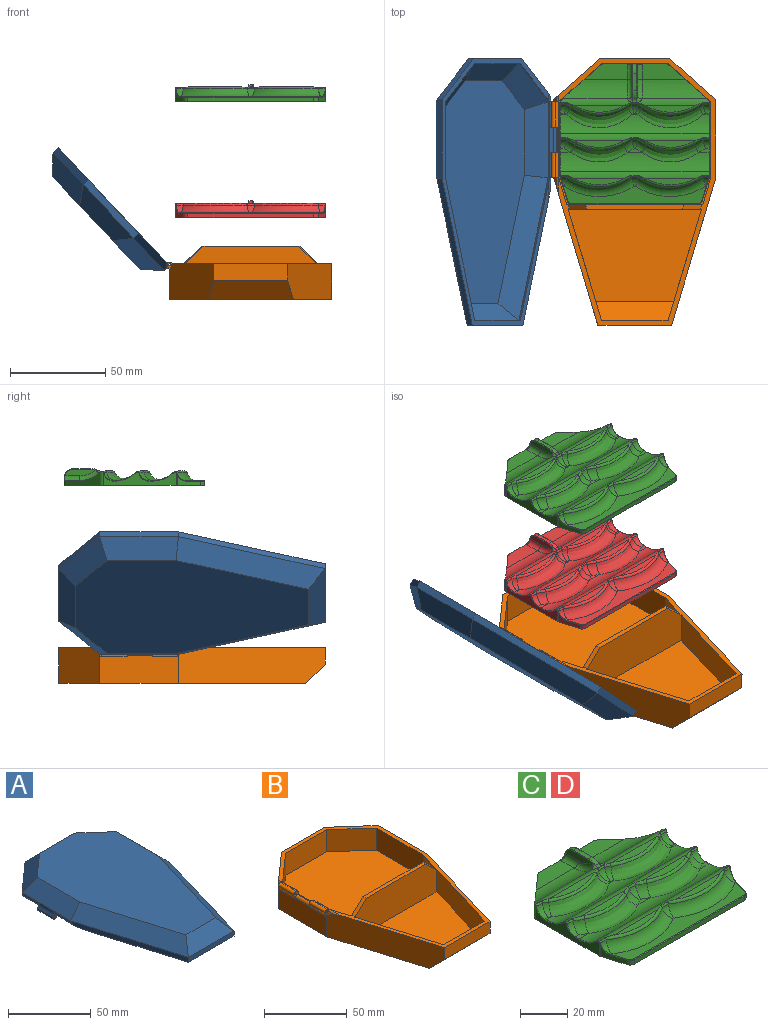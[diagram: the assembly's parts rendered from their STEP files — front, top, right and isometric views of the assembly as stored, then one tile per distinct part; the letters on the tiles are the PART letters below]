
ASSEMBLY  parts=4 mates=3
PART A: 45 faces, bbox 89.1x142.7x17.2 mm
  f0: plane 0.12x0mm, normal (0,1,0), area 0mm2, adj f8,f42
  f1: plane 0.12x0mm, normal (0,-1,0), area 0mm2, adj f8,f42
  f2: cylinder r=1.42mm len=13.33mm, axis (0,-1,0), area 61.4mm2, adj f4,f40,f41,f42
  f3: cylinder r=0.64mm len=13.33mm, axis (0,-1,0), area 53.2mm2, adj f40,f41
  f4: cylinder r=5.08mm len=13.33mm, axis (0,1,0), area 26.1mm2, adj f2,f5,f40,f41
  f5: plane 40x1.11mm, normal (1,0,0), area 43.4mm2, adj f4,f16,f22,f27,f40,f41,f43,f44
  f6: plane 140.08x81.78mm, normal (0,0,-1), area 825.5mm2, adj f7,f9,f10,f11,f12,f13,f14,f16
  f7: plane 24.08x21.4mm, normal (-0.66,0.75,0), area 115.7mm2, adj f6,f8,f14,f35,f44
  f8: plane 41.51x0.35mm, normal (-1,0,0), area 12.9mm2, adj f0,f1,f7,f9,f37,f42,f43,f44
  f9: plane 79.74x25.73mm, normal (-0.96,-0.29,0), area 289.2mm2, adj f6,f8,f10,f39,f43
  f10: plane 38.78x3.65mm, normal (0,-1,0), area 141.5mm2, adj f6,f9,f11,f38
  f11: plane 77.17x23.15mm, normal (0.96,-0.29,0), area 294.1mm2, adj f6,f10,f12,f36
  f12: plane 41.51x3.65mm, normal (1,0,0), area 151.5mm2, adj f6,f11,f13,f34
  f13: plane 24.07x21.4mm, normal (0.66,0.75,0), area 117.6mm2, adj f6,f12,f14,f32
  f14: plane 36.93x3.65mm, normal (0,1,0), area 134.8mm2, adj f6,f7,f13,f33
  f15: plane 122.3x67.3mm, normal (0,0,1), area 6472mm2, adj f32,f33,f34,f35,f36,f37,f38,f39
  f16: plane 22.64x20.14mm, normal (0.66,-0.75,0), area 33.4mm2, adj f5,f6,f17,f25,f44
  f17: plane 35x1.11mm, normal (0,-1,0), area 38.9mm2, adj f6,f16,f18,f24
  f18: plane 22.5x20mm, normal (-0.66,-0.75,0), area 33.4mm2, adj f6,f17,f19,f26
  f19: plane 40x1.11mm, normal (-1,0,0), area 44.4mm2, adj f6,f18,f20,f28
  f20: plane 75x22.5mm, normal (-0.96,0.29,0), area 86.9mm2, adj f6,f19,f21,f30
  f21: plane 35x1.11mm, normal (0,1,0), area 38.9mm2, adj f6,f20,f22,f31
  f22: plane 75.35x22.85mm, normal (0.96,0.29,0), area 86.9mm2, adj f5,f6,f21,f29,f43
  f23: plane 117.22x62.22mm, normal (0,0,-1), area 5673.4mm2, adj f24,f25,f26,f27,f28,f29,f30,f31
  f24: plane 35x8.89mm, normal (0,-0.71,-0.71), area 397.5mm2, adj f17,f23,f25,f26
  f25: plane 25.88x23.99mm, normal (0.47,-0.53,-0.71), area 332.1mm2, adj f16,f23,f24,f27
  f26: plane 25.88x23.99mm, normal (-0.47,-0.53,-0.71), area 332.1mm2, adj f18,f23,f24,f28
  f27: plane 40x8.89mm, normal (0.71,0,-0.71), area 469.6mm2, adj f5,f23,f25,f29
  f28: plane 40x8.89mm, normal (-0.71,0,-0.71), area 469.6mm2, adj f19,f23,f26,f30
  f29: plane 76.3x29.11mm, normal (0.68,0.2,-0.71), area 934.7mm2, adj f22,f23,f27,f31
  f30: plane 76.3x29.11mm, normal (-0.68,0.2,-0.71), area 934.7mm2, adj f20,f23,f28,f31
  f31: plane 35x8.89mm, normal (0,0.71,-0.71), area 356.9mm2, adj f21,f23,f29,f30
  f32: plane 27.45x25.39mm, normal (0.47,0.53,0.71), area 358.6mm2, adj f13,f15,f33,f34
  f33: plane 36.93x8.89mm, normal (0,0.71,0.71), area 421.8mm2, adj f14,f15,f32,f35
  f34: plane 41.51x8.89mm, normal (0.71,0,0.71), area 488.6mm2, adj f12,f15,f32,f36
  f35: plane 27.45x25.39mm, normal (-0.47,0.53,0.71), area 358.6mm2, adj f7,f15,f33,f37
  f36: plane 78.47x29.76mm, normal (0.68,-0.2,0.71), area 963.1mm2, adj f11,f15,f34,f38
  f37: plane 41.51x8.89mm, normal (-0.71,0,0.71), area 488.6mm2, adj f8,f15,f35,f39
  f38: plane 38.78x8.89mm, normal (0,-0.71,0.71), area 404.4mm2, adj f10,f15,f36,f39
  f39: plane 78.47x29.76mm, normal (-0.68,-0.2,0.71), area 963.1mm2, adj f9,f15,f37,f38
  f40: plane 5.49x4.09mm, normal (0,1,0), area 7.4mm2, adj f2,f3,f4,f5,f42,f44
  f41: plane 5.48x4.09mm, normal (0,-1,0), area 7.4mm2, adj f2,f3,f4,f5,f42,f43
  f42: cylinder r=5.08mm len=13.33mm, axis (0,-1,0), area 45.6mm2, adj f0,f1,f2,f8,f40,f41
  f43: bspline ~27.18x3.3mm, area 92mm2, adj f5,f6,f8,f9,f22,f41
  f44: bspline ~19.15x3.3mm, area 72.6mm2, adj f5,f6,f7,f8,f16,f40
PART B: 49 faces, bbox 86.5x140.1x27.9 mm
  f0: plane 58.42x17.53mm, normal (-0.96,0.29,0), area 943.3mm2, adj f22,f25,f31,f45,f47
  f1: plane 16.35x14.04mm, normal (0.96,0.29,0), area 239.7mm2, adj f8,f24,f31,f46
  f2: plane 5.48x3.85mm, normal (0,-1,0), area 6.5mm2, adj f3,f4,f5,f29,f32,f35,f36,f39
  f3: plane 41.51x14.93mm, normal (-1,0,0), area 599.5mm2, adj f2,f9,f10,f11,f26,f27,f28,f29
  f4: cylinder r=1.42mm len=13.33mm, axis (0,-1,0), area 54.6mm2, adj f2,f27,f29,f36
  f5: cylinder r=0.64mm len=13.33mm, axis (0,-1,0), area 53.2mm2, adj f2,f27
  f6: cylinder r=1.42mm len=13.33mm, axis (0,-1,0), area 54.6mm2, adj f9,f26,f28,f37
  f7: cylinder r=0.64mm len=13.33mm, axis (0,-1,0), area 53.2mm2, adj f9,f26
  f8: plane 40x16.35mm, normal (1,0,0), area 626.6mm2, adj f1,f17,f26,f27,f30,f31,f46
  f9: plane 5.48x3.85mm, normal (0,1,0), area 6.5mm2, adj f3,f6,f7,f28,f33,f34,f37,f38
  f10: plane 24.07x21.4mm, normal (-0.66,0.75,0), area 604.4mm2, adj f3,f16,f31,f33,f34,f38,f44
  f11: plane 77.17x23.15mm, normal (-0.96,-0.29,0), area 1457.3mm2, adj f3,f12,f31,f32,f35,f39,f44,f48
  f12: plane 38.78x8.73mm, normal (0,-1,0), area 338.5mm2, adj f11,f13,f31,f48
  f13: plane 77.17x23.15mm, normal (0.96,-0.29,0), area 1468mm2, adj f12,f14,f31,f44,f48
  f14: plane 41.51x18.89mm, normal (1,0,0), area 784.2mm2, adj f13,f15,f31,f44
  f15: plane 24.07x21.4mm, normal (0.66,0.75,0), area 608.5mm2, adj f14,f16,f31,f44
  f16: plane 36.93x18.89mm, normal (0,1,0), area 697.6mm2, adj f10,f15,f31,f44
  f17: plane 22.5x20mm, normal (0.66,-0.75,0), area 492.2mm2, adj f8,f18,f31,f46
  f18: plane 35x16.35mm, normal (0,-1,0), area 572.2mm2, adj f17,f19,f31,f46
  f19: plane 22.5x20mm, normal (-0.66,-0.75,0), area 492.2mm2, adj f18,f20,f31,f46
  f20: plane 40x16.35mm, normal (-1,0,0), area 654mm2, adj f19,f21,f31,f46
  f21: plane 16.35x14.04mm, normal (-0.96,0.29,0), area 239.7mm2, adj f20,f24,f31,f46
  f22: plane 35x6.19mm, normal (0,1,0), area 216.7mm2, adj f0,f23,f31,f47
  f23: plane 58.42x17.53mm, normal (0.96,0.29,0), area 943.3mm2, adj f22,f25,f31,f45,f47
  f24: plane 71.58x25.34mm, normal (0,1,0), area 1720.4mm2, adj f1,f21,f31,f41,f42,f43,f46
  f25: plane 70.05x25.34mm, normal (0,-1,0), area 1681.8mm2, adj f0,f23,f31,f41,f42,f43,f45
  f26: plane 5.48x3.96mm, normal (0,-1,0), area 9.4mm2, adj f3,f6,f7,f8,f28,f30,f31,f34
  f27: plane 5.48x3.96mm, normal (0,1,0), area 9.4mm2, adj f3,f4,f5,f8,f29,f30,f31,f35
  f28: cylinder r=5.08mm len=13.33mm, axis (0,-1,0), area 45.6mm2, adj f3,f6,f9,f26
  f29: cylinder r=5.08mm len=13.33mm, axis (0,-1,0), area 45.6mm2, adj f2,f3,f4,f27
  f30: plane 13.33x0.64mm, normal (0,0,1), area 8.5mm2, adj f8,f26,f27,f40
  f31: plane 140.08x82.62mm, normal (0,0,1), area 840.3mm2, adj f0,f1,f8,f10,f11,f12,f13,f14
  f32: cylinder r=5.08mm len=2.99mm, axis (0,-1,0), area 3.6mm2, adj f2,f3,f11,f39
  f33: cylinder r=5.08mm len=2.71mm, axis (0,1,0), area 3.9mm2, adj f3,f9,f10,f38
  f34: cylinder r=1.27mm len=16.66mm, axis (0,1,0), area 4.7mm2, adj f9,f10,f26,f31,f37,f38
  f35: cylinder r=1.27mm len=21.92mm, axis (0,1,0), area 10.2mm2, adj f2,f11,f27,f31,f36,f39
  f36: cylinder r=2.54mm len=13.33mm, axis (0,-1,0), area 22.6mm2, adj f2,f4,f27,f35
  f37: cylinder r=2.54mm len=13.33mm, axis (0,-1,0), area 22.6mm2, adj f6,f9,f26,f34
  f38: cylinder r=5.08mm len=2.27mm, axis (0,1,0), area 2.3mm2, adj f9,f10,f33,f34
  f39: cylinder r=5.08mm len=4.6mm, axis (0,-1,0), area 4.3mm2, adj f2,f11,f32,f35
  f40: cylinder r=1.91mm len=13.33mm, axis (0,-1,0), area 39.9mm2, adj f3,f26,f27,f30
  f41: plane 51.79x2.54mm, normal (0,0,1), area 129.6mm2, adj f24,f25,f42,f43
  f42: plane 10.15x8.99mm, normal (-0.68,-0.2,0.71), area 33.7mm2, adj f24,f25,f31,f41
  f43: plane 10.15x8.99mm, normal (0.68,-0.2,0.71), area 33.7mm2, adj f24,f25,f31,f41
  f44: plane 129.92x85.08mm, normal (0,0,-1), area 9191.4mm2, adj f3,f10,f11,f13,f14,f15,f16,f48
  f45: plane 70.05x48.26mm, normal (0,0,1), area 2682mm2, adj f0,f23,f25,f47
  f46: plane 80x74.04mm, normal (0,0,1), area 5414.1mm2, adj f1,f8,f17,f18,f19,f20,f21,f24
  f47: plane 41.1x10.16mm, normal (0,0.71,0.71), area 546.7mm2, adj f0,f22,f23,f45
  f48: plane 44.88x10.16mm, normal (0,-0.71,-0.71), area 601mm2, adj f11,f12,f13,f44
PART C: 152 faces, bbox 84.9x79x9.7 mm
  f0: plane 75.15x9.18mm, normal (0,0,1), area 389.9mm2, adj f27,f28,f29,f30,f31,f116,f119,f121
  f1: plane 12.35x5.29mm, normal (-0.96,-0.29,0), area 33.7mm2, adj f13,f82,f89,f125,f127
  f2: cylinder r=15.24mm len=34.12mm, axis (1,0,0), area 316.2mm2, adj f3,f14,f75,f148,f149
  f3: plane 22.81x8.29mm, normal (0,0,1), area 150.1mm2, adj f2,f14,f15,f85,f150,f151
  f4: plane 26.96x3.76mm, normal (0,0,1), area 67.3mm2, adj f53,f75
  f5: plane 26.91x3.64mm, normal (0,0,1), area 65.6mm2, adj f64,f65,f67,f74
  f6: plane 26.91x3.53mm, normal (0,0,1), area 64.1mm2, adj f72,f73
  f7: plane 3.32x0.83mm, normal (0,0,1), area 2.2mm2, adj f25,f42,f44,f94
  f8: plane 3.33x0.83mm, normal (0,0,1), area 1.6mm2, adj f25,f47,f48,f49
  f9: plane 5.69x2.1mm, normal (0,0,1), area 7.9mm2, adj f24,f32,f33,f126
  f10: plane 5.69x2.1mm, normal (0,0,1), area 7.9mm2, adj f24,f39,f40,f101
  f11: plane 3.32x0.83mm, normal (0,0,1), area 2.2mm2, adj f25,f41,f43,f113
  f12: plane 22.81x8.29mm, normal (0,0,1), area 150.1mm2, adj f15,f16,f26,f86,f141,f142
  f13: plane 78.73x73.79mm, normal (0,0,-1), area 5309.7mm2, adj f1,f14,f15,f16,f17,f18,f19,f81
  f14: plane 20.55x18.27mm, normal (-0.66,0.75,0), area 91.1mm2, adj f2,f3,f13,f75,f84,f85
  f15: plane 32.66x4.42mm, normal (0,1,0), area 88.9mm2, adj f3,f12,f13,f80,f85,f86,f141,f151
  f16: plane 20.55x18.27mm, normal (0.66,0.75,0), area 91.1mm2, adj f12,f13,f26,f75,f86,f87
  f17: plane 38.11x7.17mm, normal (1,0,0), area 142.3mm2, adj f13,f87,f88,f93,f94,f95,f97,f99
  f18: plane 12.35x5.29mm, normal (0.96,-0.29,0), area 33.7mm2, adj f13,f83,f88,f114,f116
  f19: plane 38.11x7.17mm, normal (-1,0,0), area 142.3mm2, adj f13,f84,f89,f111,f113,f115,f117,f122
  f20: plane 8.07x2.1mm, normal (0,0,1), area 8.8mm2, adj f24,f35,f36,f37
  f21: plane 26.96x3.76mm, normal (0,0,1), area 67.3mm2, adj f56,f75
  f22: plane 26.91x3.53mm, normal (0,0,1), area 64.1mm2, adj f69,f73
  f23: plane 26.91x3.64mm, normal (0,0,1), area 65.6mm2, adj f60,f61,f62,f74
  f24: cylinder r=15.24mm len=78.22mm, axis (1,0,0), area 659.6mm2, adj f9,f10,f20,f34,f38,f73,f102,f128
  f25: cylinder r=15.24mm len=78.22mm, axis (1,0,0), area 536.7mm2, adj f7,f8,f11,f45,f46,f74,f95,f115
  f26: cylinder r=15.24mm len=34.12mm, axis (1,0,0), area 316.2mm2, adj f12,f16,f75,f143,f144
  f27: cylinder r=5.08mm len=4.98mm, axis (1,0,0), area 14.4mm2, adj f0,f28,f68,f127,f129
  f28: torus R=33.65mm, axis (0,0,1), area 257.4mm2, adj f0,f27,f29,f69
  f29: cylinder r=5.08mm len=4.98mm, axis (1,0,0), area 15.3mm2, adj f0,f28,f30,f70
  f30: torus R=33.65mm, axis (0,0,1), area 257.4mm2, adj f0,f29,f31,f72
  f31: cylinder r=5.08mm len=4.98mm, axis (1,0,0), area 14.4mm2, adj f0,f30,f71,f112,f114
  f32: cylinder r=5.08mm len=4.98mm, axis (1,0,0), area 19.1mm2, adj f9,f33,f59,f124
  f33: torus R=33.65mm, axis (0,0,1), area 32.2mm2, adj f9,f32,f34,f60
  f34: bspline ~32.78x10.46mm, area 216.7mm2, adj f24,f33,f35,f61
  f35: torus R=33.65mm, axis (0,0,1), area 32.2mm2, adj f20,f34,f36,f62
  f36: cylinder r=5.08mm len=4.98mm, axis (1,0,0), area 15.3mm2, adj f20,f35,f37,f63
  f37: torus R=33.65mm, axis (0,0,1), area 32.2mm2, adj f20,f36,f38,f64
  f38: bspline ~32.78x10.46mm, area 216.7mm2, adj f24,f37,f39,f65
  f39: torus R=33.65mm, axis (0,0,1), area 32.2mm2, adj f10,f38,f40,f67
  f40: cylinder r=5.08mm len=4.98mm, axis (1,0,0), area 19.1mm2, adj f10,f39,f66,f100
  f41: cylinder r=5.08mm len=4.98mm, axis (1,0,0), area 20.1mm2, adj f11,f43,f52,f109,f111
  f42: cylinder r=5.08mm len=4.98mm, axis (1,0,0), area 20.1mm2, adj f7,f44,f50,f92,f93
  f43: torus R=33.65mm, axis (0,0,1), area 15.2mm2, adj f11,f41,f45,f54
  f44: torus R=33.65mm, axis (0,0,1), area 15.2mm2, adj f7,f42,f46,f51
  f45: bspline ~37.61x12.73mm, area 261.1mm2, adj f25,f43,f47,f56
  f46: bspline ~37.61x12.73mm, area 261.1mm2, adj f25,f44,f48,f53
  f47: torus R=33.65mm, axis (0,0,1), area 15.2mm2, adj f8,f45,f49,f58
  f48: torus R=33.65mm, axis (0,0,1), area 15.2mm2, adj f8,f46,f49,f55
  f49: cylinder r=5.08mm len=4.98mm, axis (1,0,0), area 15.3mm2, adj f8,f47,f48,f57
  f50: cylinder r=1.27mm len=3.69mm, axis (1,0,0), area 3.4mm2, adj f42,f51,f90,f91
  f51: torus R=27.43mm, axis (0,0,-1), area 3.9mm2, adj f44,f50,f53,f75,f90
  f52: cylinder r=1.27mm len=3.69mm, axis (1,0,0), area 3.4mm2, adj f41,f54,f105,f107
  f53: bspline ~32.79x6.3mm, area 48.7mm2, adj f4,f46,f51,f55,f75
  f54: torus R=27.43mm, axis (0,0,-1), area 3.9mm2, adj f43,f52,f56,f75,f105
  f55: torus R=27.43mm, axis (0,0,-1), area 3.9mm2, adj f48,f53,f57,f75
  f56: bspline ~32.79x6.3mm, area 48.7mm2, adj f21,f45,f54,f58,f75
  f57: cylinder r=1.27mm len=4.14mm, axis (1,0,0), area 4.2mm2, adj f49,f55,f58,f75
  f58: torus R=27.43mm, axis (0,0,-1), area 3.9mm2, adj f47,f56,f57,f75
  f59: cylinder r=1.27mm len=3.69mm, axis (1,0,0), area 3.4mm2, adj f32,f60,f118,f122
  f60: torus R=27.43mm, axis (0,0,-1), area 7.7mm2, adj f23,f33,f59,f61,f74,f118
  f61: bspline ~28.93x5.06mm, area 42.8mm2, adj f23,f34,f60,f62
  f62: torus R=27.43mm, axis (0,0,-1), area 7.8mm2, adj f23,f35,f61,f63,f74
  f63: cylinder r=1.27mm len=4.14mm, axis (1,0,0), area 4.2mm2, adj f36,f62,f64,f74
  f64: torus R=27.43mm, axis (0,0,-1), area 7.8mm2, adj f5,f37,f63,f65,f74
  f65: bspline ~28.93x5.06mm, area 42.8mm2, adj f5,f38,f64,f67
  f66: cylinder r=1.27mm len=3.69mm, axis (1,0,0), area 3.4mm2, adj f40,f67,f96,f99
  f67: torus R=27.43mm, axis (0,0,-1), area 7.7mm2, adj f5,f39,f65,f66,f74,f96
  f68: cylinder r=1.27mm len=3.69mm, axis (1,0,0), area 3.4mm2, adj f27,f69,f131,f132,f134
  f69: torus R=27.43mm, axis (0,0,-1), area 59.8mm2, adj f22,f28,f68,f70,f73,f131
  f70: cylinder r=1.27mm len=4.14mm, axis (1,0,0), area 4.2mm2, adj f29,f69,f72,f73
  f71: cylinder r=1.27mm len=3.69mm, axis (1,0,0), area 3.4mm2, adj f31,f72,f103,f108,f110
  f72: torus R=27.43mm, axis (0,0,-1), area 59.8mm2, adj f6,f30,f70,f71,f73,f103
  f73: cylinder r=5.08mm len=78.22mm, axis (1,0,0), area 262.4mm2, adj f6,f22,f24,f69,f70,f72,f103,f104
  f74: cylinder r=5.08mm len=78.22mm, axis (1,0,0), area 262.4mm2, adj f5,f23,f25,f60,f62,f63,f64,f67
  f75: cylinder r=5.08mm len=78.48mm, axis (1,0,0), area 246.4mm2, adj f2,f4,f14,f16,f21,f26,f51,f53
  f76: plane 16.21x3.56mm, normal (-1,0,0), area 44.7mm2, adj f138,f139,f140,f149,f150
  f77: plane 16.21x3.56mm, normal (1,0,0), area 44.7mm2, adj f135,f136,f137,f142,f143
  f78: plane 8.85x2.03mm, normal (0,0,1), area 18mm2, adj f79,f80,f136,f139
  f79: cylinder r=8.89mm len=4.47mm, axis (1,0,0), area 9.5mm2, adj f78,f135,f138,f146
  f80: cylinder r=5.08mm len=5.08mm, axis (-1,0,0), area 15.8mm2, adj f15,f78,f137,f140,f141,f151
  f81: plane 66.24x2.29mm, normal (0,-1,0), area 151.4mm2, adj f13,f82,f83,f121
  f82: cylinder r=2.54mm len=2.43mm, axis (0,0,1), area 7.4mm2, adj f1,f13,f81,f123
  f83: cylinder r=2.54mm len=2.43mm, axis (0,0,1), area 7.4mm2, adj f13,f18,f81,f119
  f84: cylinder r=2.54mm len=7.32mm, axis (0,0,1), area 15.1mm2, adj f13,f14,f19,f75,f107,f109
  f85: cylinder r=2.54mm len=2.54mm, axis (0,0,1), area 4.7mm2, adj f3,f13,f14,f15
  f86: cylinder r=2.54mm len=2.54mm, axis (0,0,1), area 4.7mm2, adj f12,f13,f15,f16
  f87: cylinder r=2.54mm len=7.32mm, axis (0,0,1), area 15.1mm2, adj f13,f16,f17,f75,f91,f92
  f88: cylinder r=2.54mm len=7.01mm, axis (0,0,1), area 4.6mm2, adj f13,f17,f18,f110,f112
  f89: cylinder r=2.54mm len=7.01mm, axis (0,0,1), area 4.6mm2, adj f1,f13,f19,f129,f132
  f90: cylinder r=0.25mm len=3.81mm, axis (-1,0,0), area 0.8mm2, adj f50,f51,f75,f91
  f91: bspline ~1.25x1.18mm, area 0.4mm2, adj f50,f75,f87,f90,f92
  f92: bspline ~0.33x0.31mm, area 0mm2, adj f42,f87,f91,f93
  f93: torus R=5.33mm, axis (1,0,0), area 2.8mm2, adj f17,f42,f92,f94
  f94: cylinder r=0.25mm len=0.83mm, axis (0,1,0), area 0.3mm2, adj f7,f17,f93,f95
  f95: torus R=15.49mm, axis (1,0,0), area 4.4mm2, adj f17,f25,f94,f97
  f96: cylinder r=0.25mm len=3.69mm, axis (-1,0,0), area 0.8mm2, adj f66,f67,f74,f98
  f97: torus R=4.83mm, axis (1,0,0), area 0.9mm2, adj f17,f74,f95,f98
  f98: sphere r=0.25mm, area 0.1mm2, adj f96,f97,f99
  f99: torus R=1.02mm, axis (1,0,0), area 0.3mm2, adj f17,f66,f98,f100
  f100: torus R=5.33mm, axis (1,0,0), area 2.8mm2, adj f17,f40,f99,f101
  f101: cylinder r=0.25mm len=2.1mm, axis (0,1,0), area 0.8mm2, adj f10,f17,f100,f102
  f102: torus R=15.49mm, axis (1,0,0), area 4.4mm2, adj f17,f24,f101,f104
  f103: cylinder r=0.25mm len=3.69mm, axis (-1,0,0), area 0.8mm2, adj f71,f72,f73,f106
  f104: torus R=4.83mm, axis (1,0,0), area 0.9mm2, adj f17,f73,f102,f106
  f105: cylinder r=0.25mm len=3.81mm, axis (-1,0,0), area 0.8mm2, adj f52,f54,f75,f107
  f106: sphere r=0.25mm, area 0.1mm2, adj f103,f104,f108
  f107: bspline ~1.18x1.18mm, area 0.4mm2, adj f52,f75,f84,f105,f109
  f108: torus R=1.02mm, axis (1,0,0), area 0.1mm2, adj f17,f71,f106,f110
  f109: bspline ~0.32x0.31mm, area 0mm2, adj f41,f84,f107,f111
  f110: bspline ~0.91x0.54mm, area 0.2mm2, adj f71,f88,f108,f112
  f111: torus R=5.33mm, axis (-1,0,0), area 2.8mm2, adj f19,f41,f109,f113
  f112: bspline ~2.54x1.12mm, area 0.5mm2, adj f31,f88,f110,f114
  f113: cylinder r=0.25mm len=0.83mm, axis (0,-1,0), area 0.3mm2, adj f11,f19,f111,f115
  f114: bspline ~5.94x3.59mm, area 2.2mm2, adj f18,f31,f112,f116
  f115: torus R=15.49mm, axis (-1,0,0), area 4.4mm2, adj f19,f25,f113,f117
  f116: cylinder r=0.25mm len=7.62mm, axis (0.29,0.96,0), area 3.1mm2, adj f0,f18,f114,f119
  f117: torus R=4.83mm, axis (-1,0,0), area 0.9mm2, adj f19,f74,f115,f120
  f118: cylinder r=0.25mm len=3.69mm, axis (-1,0,0), area 0.8mm2, adj f59,f60,f74,f120
  f119: torus R=2.29mm, axis (0,0,1), area 1.2mm2, adj f0,f83,f116,f121
  f120: sphere r=0.25mm, area 0.1mm2, adj f117,f118,f122
  f121: cylinder r=0.25mm len=66.24mm, axis (1,0,0), area 26.4mm2, adj f0,f81,f119,f123
  f122: torus R=1.02mm, axis (-1,0,0), area 0.3mm2, adj f19,f59,f120,f124
  f123: torus R=2.29mm, axis (0,0,1), area 1.2mm2, adj f0,f82,f121,f125
  f124: torus R=5.33mm, axis (-1,0,0), area 2.8mm2, adj f19,f32,f122,f126
  f125: cylinder r=0.25mm len=7.62mm, axis (0.29,-0.96,0), area 3.1mm2, adj f0,f1,f123,f127
  f126: cylinder r=0.25mm len=2.1mm, axis (0,-1,0), area 0.8mm2, adj f9,f19,f124,f128
  f127: bspline ~5.94x3.59mm, area 2.2mm2, adj f1,f27,f125,f129
  f128: torus R=15.49mm, axis (-1,0,0), area 4.4mm2, adj f19,f24,f126,f130
  f129: bspline ~2.54x1.12mm, area 0.5mm2, adj f27,f89,f127,f132
  f130: torus R=4.83mm, axis (-1,0,0), area 0.9mm2, adj f19,f73,f128,f133
  f131: cylinder r=0.25mm len=3.69mm, axis (-1,0,0), area 0.8mm2, adj f68,f69,f73,f133
  f132: bspline ~0.88x0.67mm, area 0.2mm2, adj f68,f89,f129,f134
  f133: sphere r=0.25mm, area 0.1mm2, adj f130,f131,f134
  f134: torus R=1.02mm, axis (-1,0,0), area 0.1mm2, adj f19,f68,f132,f133
  f135: torus R=8.64mm, axis (-1,0,0), area 1.6mm2, adj f77,f79,f136,f144,f145
  f136: cylinder r=0.25mm len=8.85mm, axis (0,-1,0), area 3.5mm2, adj f77,f78,f135,f137
  f137: torus R=4.83mm, axis (-1,0,0), area 2.7mm2, adj f77,f80,f136,f141
  f138: torus R=8.64mm, axis (-1,0,0), area 1.6mm2, adj f76,f79,f139,f147,f148
  f139: cylinder r=0.25mm len=8.85mm, axis (0,1,0), area 3.5mm2, adj f76,f78,f138,f140
  f140: torus R=4.83mm, axis (-1,0,0), area 2.7mm2, adj f76,f80,f139,f151
  f141: bspline ~5.31x3.18mm, area 1.7mm2, adj f12,f15,f80,f137,f142
  f142: cylinder r=2.54mm len=7.87mm, axis (0,1,0), area 31.4mm2, adj f12,f77,f141,f143
  f143: torus R=12.7mm, axis (-1,0,0), area 40.9mm2, adj f26,f77,f142,f144
  f144: bspline ~2.55x1.95mm, area 0.2mm2, adj f26,f135,f143,f145
  f145: bspline ~4.04x2.93mm, area 6.3mm2, adj f75,f135,f144,f146
  f146: cylinder r=2.54mm len=2.03mm, axis (1,0,0), area 4.1mm2, adj f75,f79,f145,f147
  f147: bspline ~3.82x3.3mm, area 6.3mm2, adj f75,f138,f146,f148
  f148: bspline ~2.6x2.05mm, area 0.2mm2, adj f2,f138,f147,f149
  f149: torus R=12.7mm, axis (-1,0,0), area 40.9mm2, adj f2,f76,f148,f150
  f150: cylinder r=2.54mm len=7.87mm, axis (0,-1,0), area 31.4mm2, adj f3,f76,f149,f151
  f151: bspline ~5.26x3.14mm, area 1.7mm2, adj f3,f15,f80,f140,f150
PART D: same geometry as C
PLACE A rot(axis=(0,-1,0),133.3deg) t=(-19.01,26.95,-42.88)mm
PLACE B rot(axis=(0.71,0.21,-0.67),0deg) t=(62.29,26.95,-77.98)mm fixed
PLACE C rot(axis=(0.71,0.21,-0.67),0deg) t=(-26.35,27.38,21.08)mm
PLACE D t=(-26.35,27.38,-40.12)mm
MATE slider C.f13 <-> B.f46  axis (0,0,-1) through (62.29,122.76,21.08)mm
MATE revolute A.f2 <-> B.f4  axis (0,-1,0) through (19.75,115.28,-64.81)mm
MATE slider D.f13 <-> B.f46  axis (0,0,-1) through (62.29,122.76,-40.12)mm
